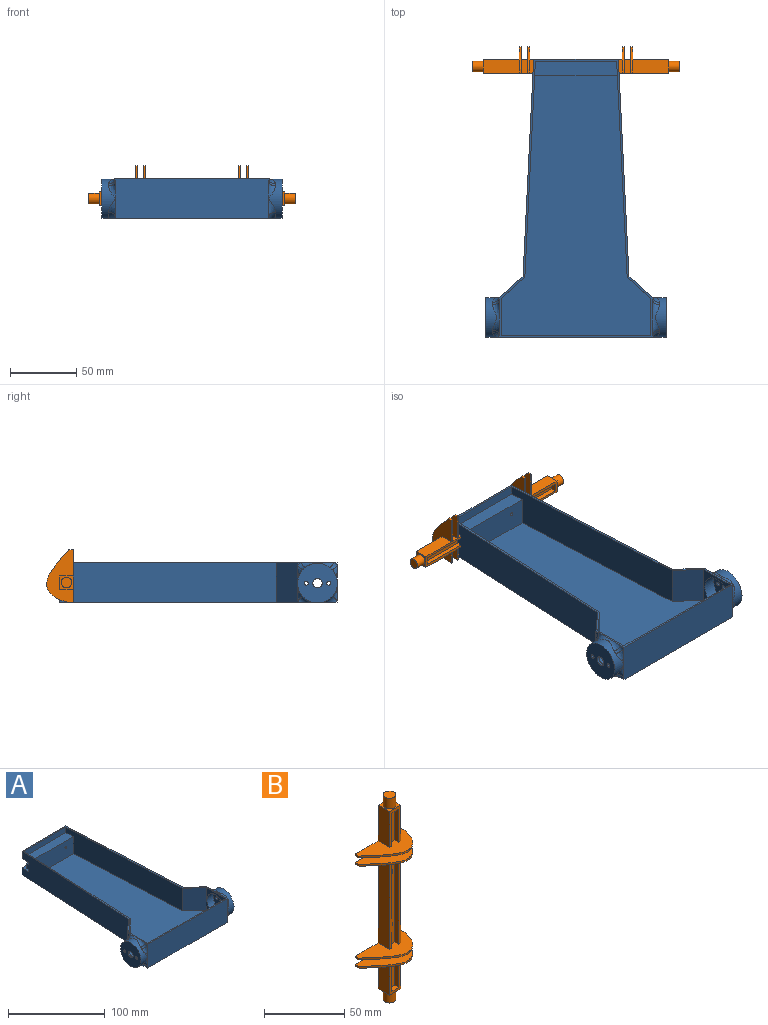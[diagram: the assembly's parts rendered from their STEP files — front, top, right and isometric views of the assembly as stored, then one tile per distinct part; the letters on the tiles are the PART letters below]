
ASSEMBLY  parts=2 mates=1
PART A: 75 faces, bbox 136.9x215.1x43.9 mm
  f0: plane 64x9.1mm, normal (0,1,0), area 582.4mm2, adj f1,f2,f15,f60
  f1: plane 164x30mm, normal (1,0.05,0), area 4827.5mm2, adj f0,f15,f21,f22,f26,f60,f61,f62
  f2: plane 164x30mm, normal (-1,0.05,0), area 4827.5mm2, adj f0,f15,f22,f25,f26,f60,f61,f62
  f3: plane 61.33x7.1mm, normal (0,-1,0), area 435.5mm2, adj f4,f5,f26,f59
  f4: plane 163.26x28.6mm, normal (-1,-0.05,0), area 4446.5mm2, adj f3,f6,f23,f26,f58,f59
  f5: plane 163.26x28.6mm, normal (1,-0.05,0), area 4446.5mm2, adj f3,f6,f24,f26,f58,f59
  f6: plane 196.6x113.2mm, normal (0,0,1), area 15345mm2, adj f4,f5,f16,f17,f18,f23,f24,f58
  f7: plane 2.24x2.17mm, normal (-1,0,0), area 2.3mm2, adj f19,f26,f52
  f8: plane 1.37x1.33mm, normal (-1,0,0), area 0.9mm2, adj f15,f25,f57
  f9: plane 2.24x2.17mm, normal (-1,0,0), area 2.3mm2, adj f25,f26,f54
  f10: plane 1.37x1.33mm, normal (-1,0,0), area 0.9mm2, adj f15,f19,f49
  f11: plane 2.24x2.17mm, normal (1,0,0), area 2.3mm2, adj f19,f26,f37
  f12: cylinder r=13.2mm len=26.4mm, axis (1,0,0), area 779.6mm2, adj f18,f33
  f13: plane 1.37x1.33mm, normal (1,0,0), area 0.9mm2, adj f15,f21,f42
  f14: plane 2.24x2.17mm, normal (1,0,0), area 2.3mm2, adj f21,f26,f39
  f15: plane 210.93x136.93mm, normal (0,0,-1), area 17051.4mm2, adj f0,f1,f2,f8,f10,f13,f19,f20
  f16: plane 28.6x27.97mm, normal (1,0,0), area 252.6mm2, adj f6,f17,f24,f26,f27
  f17: plane 113.2x28.6mm, normal (0,1,0), area 3237.5mm2, adj f6,f16,f18,f26
  f18: plane 28.6x27.97mm, normal (-1,0,0), area 252.6mm2, adj f6,f12,f17,f23,f26
  f19: plane 116.49x30.49mm, normal (0,-1,0), area 3480mm2, adj f7,f10,f11,f15,f20,f26,f35,f36
  f20: plane 1.37x1.33mm, normal (1,0,0), area 0.9mm2, adj f15,f19,f34
  f21: plane 30.49x18.49mm, normal (0.66,0.75,0), area 722.5mm2, adj f1,f13,f14,f15,f26,f40,f41
  f22: plane 64x9.1mm, normal (0,1,0), area 582.4mm2, adj f1,f2,f26,f66
  f23: plane 28.6x17.97mm, normal (-0.66,-0.75,0), area 687.6mm2, adj f4,f6,f18,f26
  f24: plane 28.6x17.97mm, normal (0.66,-0.75,0), area 687.6mm2, adj f5,f6,f16,f26
  f25: plane 30.49x18.49mm, normal (-0.66,0.75,0), area 722.5mm2, adj f2,f8,f9,f15,f26,f55,f56
  f26: plane 210.74x116.74mm, normal (0,0,1), area 855.4mm2, adj f1,f2,f3,f4,f5,f7,f9,f11
  f27: cylinder r=13.2mm len=26.4mm, axis (1,0,0), area 779.6mm2, adj f16,f48
  f28: cylinder r=15mm len=30mm, axis (-1,0,0), area 549.7mm2, adj f15,f29,f34,f35,f36,f37,f38,f39
  f29: plane 30x29.6mm, normal (1,0,0), area 652.4mm2, adj f15,f28,f30,f31,f32
  f30: cylinder r=1.5mm len=3mm, axis (1,0,0), area 18.8mm2, adj f29,f33
  f31: cylinder r=1.5mm len=3mm, axis (1,0,0), area 18.8mm2, adj f29,f33
  f32: cylinder r=3.5mm len=7mm, axis (1,0,0), area 44mm2, adj f29,f33
  f33: plane 26.4x26.4mm, normal (-1,0,0), area 494.8mm2, adj f12,f30,f31,f32
  f34: torus R=20mm, axis (-1,0,0), area 45.3mm2, adj f15,f20,f28,f35
  f35: bspline ~13.78x5.36mm, area 42.2mm2, adj f19,f28,f34
  f36: bspline ~13.78x5.36mm, area 42.2mm2, adj f19,f28,f37
  f37: torus R=20mm, axis (-1,0,0), area 20.6mm2, adj f11,f28,f36,f38
  f38: bspline ~26.72x5.48mm, area 93.6mm2, adj f26,f28,f37,f39
  f39: torus R=20mm, axis (-1,0,0), area 20.6mm2, adj f14,f28,f38,f40
  f40: bspline ~13.78x5.36mm, area 42.2mm2, adj f21,f28,f39
  f41: bspline ~13.78x5.36mm, area 42.2mm2, adj f21,f28,f42
  f42: torus R=20mm, axis (-1,0,0), area 45.3mm2, adj f13,f15,f28,f41
  f43: cylinder r=15mm len=30mm, axis (1,0,0), area 549.7mm2, adj f15,f44,f49,f50,f51,f52,f53,f54
  f44: plane 30x29.6mm, normal (-1,0,0), area 652.4mm2, adj f15,f43,f45,f46,f47
  f45: cylinder r=1.5mm len=3mm, axis (-1,0,0), area 18.8mm2, adj f44,f48
  f46: cylinder r=1.5mm len=3mm, axis (-1,0,0), area 18.8mm2, adj f44,f48
  f47: cylinder r=3.5mm len=7mm, axis (-1,0,0), area 44mm2, adj f44,f48
  f48: plane 26.4x26.4mm, normal (1,0,0), area 494.8mm2, adj f27,f45,f46,f47
  f49: torus R=20mm, axis (1,0,0), area 45.3mm2, adj f10,f15,f43,f50
  f50: bspline ~13.78x5.36mm, area 42.2mm2, adj f19,f43,f49
  f51: bspline ~13.78x5.36mm, area 42.2mm2, adj f19,f43,f52
  f52: torus R=20mm, axis (1,0,0), area 20.6mm2, adj f7,f43,f51,f53
  f53: bspline ~26.72x5.48mm, area 93.6mm2, adj f26,f43,f52,f54
  f54: torus R=20mm, axis (1,0,0), area 20.6mm2, adj f9,f43,f53,f55
  f55: bspline ~13.78x5.36mm, area 42.2mm2, adj f25,f43,f54
  f56: bspline ~13.78x5.36mm, area 42.2mm2, adj f25,f43,f57
  f57: torus R=20mm, axis (1,0,0), area 45.3mm2, adj f8,f15,f43,f56
  f58: plane 62.37x21.5mm, normal (0,-1,0), area 1331.9mm2, adj f4,f5,f6,f59,f67,f68
  f59: plane 62.37x10.6mm, normal (0,0,1), area 655.6mm2, adj f3,f4,f5,f58
  f60: plane 64.98x10mm, normal (0,0,1), area 644.9mm2, adj f0,f1,f2,f61
  f61: plane 64.98x2.6mm, normal (0,1,0), area 168.9mm2, adj f1,f2,f60,f62
  f62: plane 64.98x3mm, normal (0,0,-1), area 194.5mm2, adj f1,f2,f61,f63
  f63: plane 64.68x6.6mm, normal (0,1,0), area 417.9mm2, adj f1,f2,f62,f64,f67,f68
  f64: plane 64.98x3mm, normal (0,0,1), area 194.5mm2, adj f1,f2,f63,f65
  f65: plane 64.98x2.6mm, normal (0,1,0), area 168.9mm2, adj f1,f2,f64,f66
  f66: plane 64.98x10mm, normal (0,0,-1), area 644.9mm2, adj f1,f2,f22,f65
  f67: cylinder r=1.2mm len=5mm, axis (0,1,0), area 37.7mm2, adj f58,f63
  f68: cylinder r=1.2mm len=5mm, axis (0,1,0), area 37.7mm2, adj f58,f63
  f69: plane 62.17x5.7mm, normal (0,1,0), area 354.4mm2, adj f70,f71,f72,f73
  f70: plane 62.17x8.6mm, normal (0,0,-1), area 531.1mm2, adj f69,f72,f73,f74
  f71: plane 62.17x8.6mm, normal (0,0,1), area 531.1mm2, adj f69,f72,f73,f74
  f72: plane 8.6x5.7mm, normal (1,-0.05,0), area 49.1mm2, adj f69,f70,f71,f74
  f73: plane 8.6x5.7mm, normal (-1,-0.05,0), area 49.1mm2, adj f69,f70,f71,f74
  f74: plane 61.33x5.7mm, normal (0,-1,0), area 349.6mm2, adj f70,f71,f72,f73
PART B: 73 faces, bbox 40x20.9x156 mm
  f0: plane 6x5mm, normal (0,-1,0), area 30mm2, adj f3,f5,f64,f66
  f1: plane 25.2x6mm, normal (0,-1,0), area 151.2mm2, adj f30,f32,f48,f63
  f2: plane 70x3.5mm, normal (1,0,0), area 245mm2, adj f6,f19,f31,f68
  f3: plane 5x3.5mm, normal (1,0,0), area 17.5mm2, adj f0,f8,f64,f66
  f4: plane 70x3.5mm, normal (-1,0,0), area 245mm2, adj f7,f19,f31,f68
  f5: plane 5x3.5mm, normal (-1,0,0), area 17.5mm2, adj f0,f9,f64,f66
  f6: plane 70x2mm, normal (0,-1,0), area 140mm2, adj f2,f12,f19,f68
  f7: plane 70x2mm, normal (0,-1,0), area 140mm2, adj f4,f10,f19,f68
  f8: plane 5x2mm, normal (0,-1,0), area 10mm2, adj f3,f13,f64,f66
  f9: plane 5x2mm, normal (0,-1,0), area 10mm2, adj f5,f11,f64,f66
  f10: plane 70x10mm, normal (1,0,0), area 700mm2, adj f7,f15,f19,f68
  f11: plane 10x5mm, normal (1,0,0), area 50mm2, adj f9,f15,f64,f66
  f12: plane 70x10mm, normal (-1,0,0), area 700mm2, adj f6,f15,f19,f68
  f13: plane 10x5mm, normal (-1,0,0), area 50mm2, adj f8,f15,f64,f66
  f14: plane 10x10mm, normal (0,0,-1), area 49.7mm2, adj f15,f42,f43,f44,f56
  f15: plane 140x40mm, normal (0,1,0), area 752mm2, adj f10,f11,f12,f13,f14,f17,f18,f19
  f16: plane 2.98x1.4mm, normal (0,-1,0), area 4.2mm2, adj f17,f19,f53,f54
  f17: plane 40x20.9mm, normal (0,0,-1), area 487.2mm2, adj f15,f16,f18,f23,f24,f25,f26,f27
  f18: plane 3.18x1.4mm, normal (-1,0,0), area 4.5mm2, adj f15,f17,f19,f54
  f19: plane 40x20.9mm, normal (0,0,1), area 487.2mm2, adj f2,f4,f6,f7,f10,f12,f15,f16
  f20: plane 2.98x1.4mm, normal (0,-1,0), area 4.2mm2, adj f21,f22,f51,f52
  f21: plane 40x20.9mm, normal (0,0,1), area 487.2mm2, adj f15,f20,f23,f24,f25,f26,f27,f28
  f22: plane 40x20.9mm, normal (0,0,-1), area 487.2mm2, adj f15,f20,f36,f37,f38,f42,f43,f44
  f23: plane 5x2mm, normal (0,-1,0), area 10mm2, adj f17,f21,f26,f28
  f24: plane 5x3.5mm, normal (1,0,0), area 17.5mm2, adj f17,f21,f25,f27
  f25: plane 6x5mm, normal (0,-1,0), area 30mm2, adj f17,f21,f24,f26
  f26: plane 5x3.5mm, normal (-1,0,0), area 17.5mm2, adj f17,f21,f23,f25
  f27: plane 5x2mm, normal (0,-1,0), area 10mm2, adj f17,f21,f24,f29
  f28: plane 10x5mm, normal (1,0,0), area 50mm2, adj f15,f17,f21,f23
  f29: plane 10x5mm, normal (-1,0,0), area 50mm2, adj f15,f17,f21,f27
  f30: plane 25.2x3.5mm, normal (1,0,0), area 88.2mm2, adj f1,f33,f48,f63
  f31: plane 70x6mm, normal (0,-1,0), area 405.9mm2, adj f2,f4,f19,f68,f71,f72
  f32: plane 25.2x3.5mm, normal (-1,0,0), area 88.2mm2, adj f1,f33,f48,f63
  f33: plane 27.2x10mm, normal (0,-1,0), area 120.8mm2, adj f30,f32,f34,f35,f45,f48,f63
  f34: plane 27.2x10mm, normal (1,0,0), area 272mm2, adj f15,f33,f45,f63
  f35: plane 27.2x10mm, normal (-1,0,0), area 272mm2, adj f15,f33,f45,f63
  f36: plane 25.2x3.5mm, normal (1,0,0), area 88.2mm2, adj f22,f37,f42,f58
  f37: plane 25.2x6mm, normal (0,-1,0), area 151.2mm2, adj f22,f36,f38,f58
  f38: plane 25.2x3.5mm, normal (-1,0,0), area 88.2mm2, adj f22,f37,f42,f58
  f39: plane 136x3.5mm, normal (-1,0,0), area 476mm2, adj f15,f40,f49,f57
  f40: plane 136x6mm, normal (0,1,0), area 801.9mm2, adj f39,f41,f49,f57,f71,f72
  f41: plane 136x3.5mm, normal (1,0,0), area 476mm2, adj f15,f40,f49,f57
  f42: plane 27.2x10mm, normal (0,-1,0), area 120.8mm2, adj f14,f22,f36,f38,f43,f44,f58
  f43: plane 27.2x10mm, normal (1,0,0), area 272mm2, adj f14,f15,f22,f42
  f44: plane 27.2x10mm, normal (-1,0,0), area 272mm2, adj f14,f15,f22,f42
  f45: plane 10x10mm, normal (0,0,1), area 49.7mm2, adj f15,f33,f34,f35,f46
  f46: cylinder r=4mm len=8mm, axis (0,0,-1), area 201.1mm2, adj f45,f47
  f47: plane 8x8mm, normal (0,0,1), area 50.3mm2, adj f46
  f48: plane 6x3.5mm, normal (0,0,-1), area 21mm2, adj f1,f30,f32,f33
  f49: plane 6x3.5mm, normal (0,0,-1), area 21mm2, adj f15,f39,f40,f41
  f50: plane 3.18x1.4mm, normal (-1,0,0), area 4.5mm2, adj f15,f21,f22,f52
  f51: extruded ~20x12.47mm, area 35.5mm2, adj f15,f20,f21,f22
  f52: extruded ~24.56x16.82mm, area 42.1mm2, adj f20,f21,f22,f50
  f53: extruded ~20x12.47mm, area 35.5mm2, adj f15,f16,f17,f19
  f54: extruded ~24.56x16.82mm, area 42.1mm2, adj f16,f17,f18,f19
  f55: plane 8x8mm, normal (0,0,-1), area 50.3mm2, adj f56
  f56: cylinder r=4mm len=8mm, axis (0,0,1), area 201.1mm2, adj f14,f55
  f57: plane 6x3.5mm, normal (0,0,1), area 21mm2, adj f15,f39,f40,f41
  f58: plane 6x3.5mm, normal (0,0,1), area 21mm2, adj f36,f37,f38,f42
  f59: extruded ~24.56x16.82mm, area 42.1mm2, adj f60,f62,f63,f64
  f60: plane 3.18x1.4mm, normal (-1,0,0), area 4.5mm2, adj f15,f59,f63,f64
  f61: extruded ~20x12.47mm, area 35.5mm2, adj f15,f62,f63,f64
  f62: plane 2.98x1.4mm, normal (0,-1,0), area 4.2mm2, adj f59,f61,f63,f64
  f63: plane 40x20.9mm, normal (0,0,1), area 487.2mm2, adj f1,f15,f30,f32,f33,f34,f35,f59
  f64: plane 40x20.9mm, normal (0,0,-1), area 487.2mm2, adj f0,f3,f5,f8,f9,f11,f13,f15
  f65: plane 2.98x1.4mm, normal (0,-1,0), area 4.2mm2, adj f66,f68,f69,f70
  f66: plane 40x20.9mm, normal (0,0,1), area 487.2mm2, adj f0,f3,f5,f8,f9,f11,f13,f15
  f67: plane 3.18x1.4mm, normal (-1,0,0), area 4.5mm2, adj f15,f66,f68,f70
  f68: plane 40x20.9mm, normal (0,0,-1), area 487.2mm2, adj f2,f4,f6,f7,f10,f12,f15,f31
  f69: extruded ~20x12.47mm, area 35.5mm2, adj f15,f65,f66,f68
  f70: extruded ~24.56x16.82mm, area 42.1mm2, adj f65,f66,f67,f68
  f71: cylinder r=1.5mm len=3mm, axis (0,-1,0), area 28.3mm2, adj f31,f40
  f72: cylinder r=1.5mm len=3mm, axis (0,-1,0), area 28.3mm2, adj f31,f40
PLACE A t=(0.3,-47.05,-13.37)mm fixed
PLACE B rot(axis=(0.71,0,-0.71),180deg) t=(0.3,157.45,1.63)mm
MATE fastened B.f72 <-> A.f67  axis (0,-1,0) through (-19.7,155.95,1.63)mm
